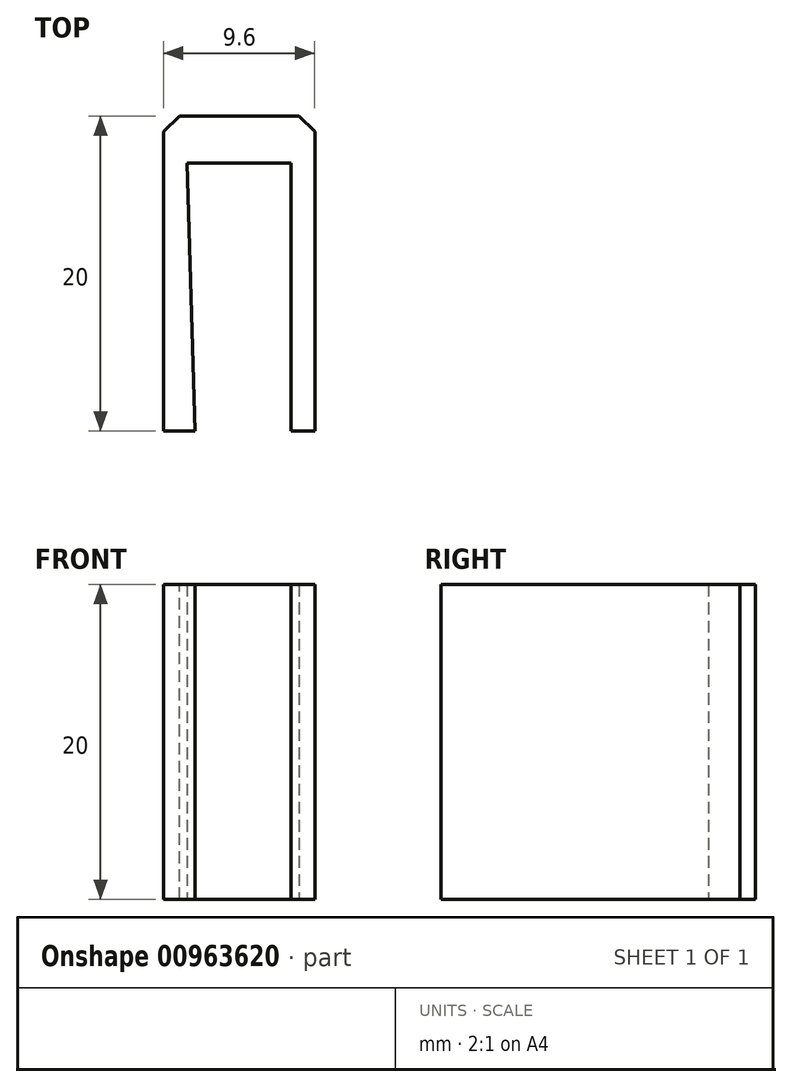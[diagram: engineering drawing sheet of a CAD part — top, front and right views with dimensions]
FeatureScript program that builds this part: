
annotation { "Feature Type Name" : "Feature", "Feature Type Description" : "" }
export const myFeature = defineFeature(function(context is Context, id is Id, definition is map)
    precondition{}
    {
        {
            var Q0;
            Q0=qCreatedBy(makeId("Top.planeOp"),FACE);
            var sketch = newSketch(context, id + "F0", { "sketchPlane" : qUnion([Q0])});
            skLineSegment(sketch, "E0", {"start": v(-33.94, -23.13) * mm, "end": v(-33.94, -3.13) * mm});
            skLineSegment(sketch, "E1", {"start": v(-33.94, -23.13) * mm, "end": v(-31.94, -23.13) * mm});
            skLineSegment(sketch, "E2", {"start": v(-31.94, -23.13) * mm, "end": v(-32.44, -6.13) * mm});
            skLineSegment(sketch, "E3", {"start": v(-33.94, -3.13) * mm, "end": v(-24.34, -3.13) * mm});
            skLineSegment(sketch, "E4", {"start": v(-25.84, -23.13) * mm, "end": v(-24.34, -23.13) * mm});
            skLineSegment(sketch, "E5", {"start": v(-25.84, -23.13) * mm, "end": v(-25.84, -6.13) * mm});
            skLineSegment(sketch, "E6", {"start": v(-25.84, -6.13) * mm, "end": v(-32.44, -6.13) * mm});
            skLineSegment(sketch, "E7", {"start": v(-24.34, -23.13) * mm, "end": v(-24.34, -3.13) * mm});
            skSolve(sketch);
        }
        {
            var Q0;
            Q0=qSketchRegion(id+"F0",true);
            extrude(context, id + "F1", {"entities" : qUnion([Q0]), "endBound" : BoundingType.SYMMETRIC, "depth" : 20 * mm, "offsetDistance" : 25 * mm});
        }
        {
            var Q0;
            Q0=makeQuery(id+"F1.opExtrude","SWEPT_EDGE",EDGE,{"disambiguationData":[OSD([sQuery(id+"F0.wireOp",EDGE,"E0"),sQuery(id+"F0.wireOp",EDGE,"E3")])]});
            var Q1;
            Q1=makeQuery(id+"F1.opExtrude","SWEPT_EDGE",EDGE,{"disambiguationData":[OSD([sQuery(id+"F0.wireOp",EDGE,"E3"),sQuery(id+"F0.wireOp",EDGE,"E7")])]});
            chamfer(context, id + "F2", {"entities" : qUnion([Q0, Q1]), "width" : 1 * mm, "tangentPropagation" : true});
        }
    });
